# Revit family: 306_589e3873ef7c4ed4a5c5665ae1d329
name_source: partatom
category: Pipe Accessories
units: mm (PartAtom-declared; Revit-internal decimal feet)

## family parameters
Always vertical = Yes
Cut with Voids When Loaded = No
Part Type = Valve - Breaks Into
Round Connector Dimension = Use Diameter
Shared = No
Work Plane-Based = No

## types (4) — shared parameters
B1 = 68 mm
B2 = 66 mm
CAT0 = Yes
Description = 3-way motorized zone valve ZRS234, PN16 internal thread
H1 = 20 mm  [stored 0.0656168 ft]
L1 = 91 mm
L2 = 89 mm
L2D_Min = 3048 mm
Manufacturer = ESBE
QmdConnectorList = 301;D;302;D
R5 = 3 mm  [stored 0.00984252 ft]
R6 = 5 mm  [stored 0.0164042 ft]
R7 = 4 mm  [stored 0.0131234 ft]
URL = http://www.esbe.eu
X2 = 2 mm  [stored 0.00656168 ft]
magiPartTypeId = 306
magiProductFamilyId = 589e3873ef7c4ed4a5c5665ae1d329

## per-type parameters (varying)
- ZRS234 230VAC 2-P 15-3.2 G1/2: C=29 mm  [stored 0.0951444 ft]; C1=22 mm; CenSd_R8_6=11 mm; D=15 mm; DT2=8 mm  [stored 0.0262467 ft]; L2D=80 mm; L5=11 mm; LT2=40 mm  [stored 0.131234 ft]; LT4=20 mm  [stored 0.0656168 ft]; R1=7 mm  [stored 0.0229659 ft]; R2=18 mm  [stored 0.0590551 ft]; R3=16 mm  [stored 0.0524934 ft]; R4=13 mm; R8=13 mm; W2D=15 mm  [stored 0.0492126 ft]; X1=14 mm  [stored 0.0459318 ft]; X1__ve=-14 mm  [stored -0.0459318 ft]; X3=48 mm  [stored 0.15748 ft]; Z3=33 mm  [stored 0.108268 ft]; Z4=2 mm  [stored 0.00656168 ft]; Z5=4 mm  [stored 0.0131234 ft]; Z6=10 mm  [stored 0.0328084 ft]; Z7=23 mm; Z9=7 mm  [stored 0.0229659 ft]; magiProductCode=ZRS234 230VAC 2-P 15-3.2 G1/2"; magiProductId=fc14a2fb676a4fad945c0fdd9d8b3f
- ZRS234 230VAC 2-P 32-8.4 G11/4: C=45 mm; C1=34 mm  [stored 0.111549 ft]; CenSd_R8_6=15 mm  [stored 0.0492126 ft]; D=32 mm; DT2=16 mm  [stored 0.0524934 ft]; L2D=105 mm; L5=16 mm  [stored 0.0524934 ft]; LT2=53 mm; LT4=26 mm  [stored 0.0853018 ft]; R1=14 mm  [stored 0.0459318 ft]; R2=24 mm  [stored 0.0787402 ft]; R3=21 mm  [stored 0.0688976 ft]; R4=18 mm  [stored 0.0590551 ft]; R8=17 mm  [stored 0.0557743 ft]; W2D=32 mm  [stored 0.104987 ft]; X1=18 mm  [stored 0.0590551 ft]; X1__ve=-18 mm  [stored -0.0590551 ft]; X3=64 mm; Z3=51 mm; Z4=3 mm  [stored 0.00984252 ft]; Z5=7 mm  [stored 0.0229659 ft]; Z6=5 mm  [stored 0.0164042 ft]; Z7=21 mm  [stored 0.0688976 ft]; Z9=11 mm; magiProductCode=ZRS234 230VAC 2-P 32-8.4 G11/4"; magiProductId=4f86806ede3040ff9e375769d02dcc
- ZRS234 230VAC 2-P 25-5.7 G1: C=37 mm; C1=28 mm  [stored 0.0918635 ft]; CenSd_R8_6=13 mm; D=25 mm; DT2=13 mm; L2D=93 mm; L5=14 mm  [stored 0.0459318 ft]; LT2=47 mm; LT4=23 mm; R1=11 mm; R2=21 mm  [stored 0.0688976 ft]; R3=19 mm; R4=16 mm  [stored 0.0524934 ft]; R8=15 mm  [stored 0.0492126 ft]; W2D=25 mm  [stored 0.082021 ft]; X1=16 mm  [stored 0.0524934 ft]; X1__ve=-16 mm; X3=56 mm; Z3=42 mm  [stored 0.137795 ft]; Z4=3 mm  [stored 0.00984252 ft]; Z5=6 mm  [stored 0.019685 ft]; Z6=4 mm  [stored 0.0131234 ft]; Z7=18 mm  [stored 0.0590551 ft]; Z9=9 mm  [stored 0.0295276 ft]; magiProductCode=ZRS234 230VAC 2-P 25-5.7 G1"; magiProductId=90c4b8ca735f4c2395a59c7d3d8b3b
- ZRS234 230VAC 2-P 20-4.6 G3/4: C=32 mm  [stored 0.104987 ft]; C1=24 mm  [stored 0.0787402 ft]; CenSd_R8_6=13 mm; D=20 mm; DT2=10 mm  [stored 0.0328084 ft]; L2D=89 mm; L5=13 mm; LT2=45 mm; LT4=22 mm; R1=9 mm  [stored 0.0295276 ft]; R2=20 mm  [stored 0.0656168 ft]; R3=18 mm  [stored 0.0590551 ft]; R4=15 mm  [stored 0.0492126 ft]; R8=14 mm  [stored 0.0459318 ft]; W2D=20 mm  [stored 0.0656168 ft]; X1=16 mm  [stored 0.0524934 ft]; X1__ve=-16 mm; X3=54 mm; Z3=36 mm  [stored 0.11811 ft]; Z4=2 mm  [stored 0.00656168 ft]; Z5=5 mm  [stored 0.0164042 ft]; Z6=8 mm  [stored 0.0262467 ft]; Z7=20 mm  [stored 0.0656168 ft]; Z9=8 mm  [stored 0.0262467 ft]; magiProductCode=ZRS234 230VAC 2-P 20-4.6 G3/4"; magiProductId=6fd52971fd06429e83e9448d0aaae3

note: [stored X ft] marks values corroborated as IEEE doubles in the binary element streams (Revit-internal decimal feet)

## geometry (parser evidence)
native form markers: Sweep x2
no freeform markers — native parametric forms only
